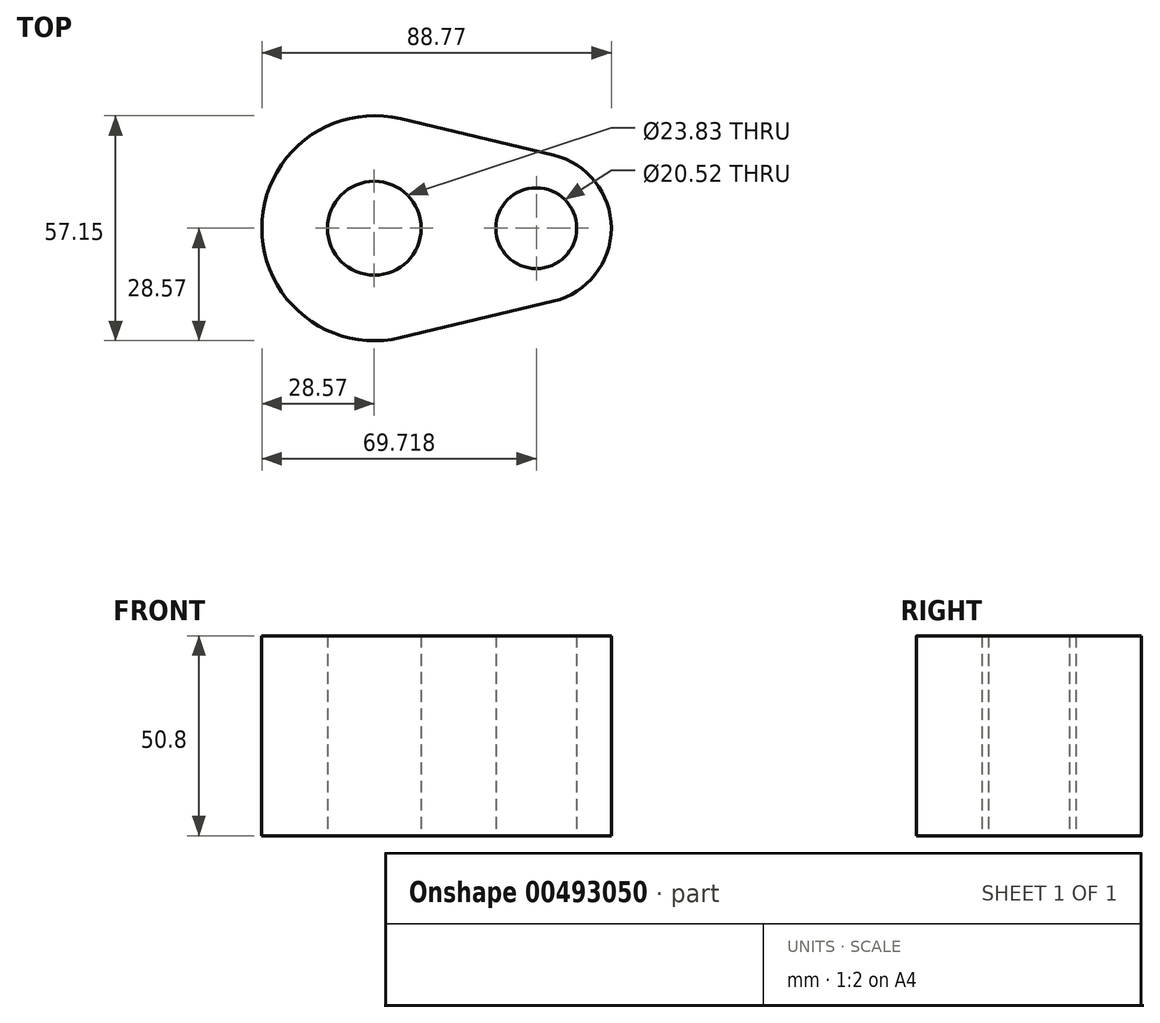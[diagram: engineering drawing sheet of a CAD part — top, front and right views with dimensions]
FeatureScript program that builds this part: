
annotation { "Feature Type Name" : "Feature", "Feature Type Description" : "" }
export const myFeature = defineFeature(function(context is Context, id is Id, definition is map)
    precondition{}
    {
        {
            var Q0;
            Q0=qCreatedBy(makeId("Top.planeOp"),FACE);
            var sketch = newSketch(context, id + "F0", { "sketchPlane" : qUnion([Q0])});
            skArc(sketch, "E0", {"start": v(6.61, 27.8) * mm, "mid": v(-28.57, 0) * mm, "end": v(6.61, -27.8) * mm});
            skArc(sketch, "E1", {"start": v(45.56, -18.53) * mm, "mid": v(60.2, 0) * mm, "end": v(45.56, 18.53) * mm});
            skLineSegment(sketch, "E2", {"start": v(6.61, 27.8) * mm, "end": v(45.56, 18.53) * mm});
            skLineSegment(sketch, "E3", {"start": v(6.61, -27.8) * mm, "end": v(45.56, -18.53) * mm});
            skCircle(sketch, "E4", {"center": v(0, 0) * mm, "radius": 11.92 * mm});
            skCircle(sketch, "E5", {"center": v(41.15, 0) * mm, "radius": 10.26 * mm});
            skSolve(sketch);
        }
        {
            var Q0;
            Q0 = qSketchRegion(id + "F0", true);
            extrude(context, id + "F1", {"entities" : qUnion([Q0]), "depth" : 25.4 * mm, "offsetDistance" : 25.4 * mm});
        }
        {
            var Q0;
            Q0=makeQuery(id+"F1.opExtrude","CAP_FACE",FACE,{"disambiguationData":[OSD([sQuery(id+"F0.wireOp",EDGE,"E0"),sQuery(id+"F0.wireOp",EDGE,"E1"),sQuery(id+"F0.wireOp",EDGE,"E2"),sQuery(id+"F0.wireOp",EDGE,"E3"),sQuery(id+"F0.wireOp",EDGE,"E4"),sQuery(id+"F0.wireOp",EDGE,"E5")])],"isStart":false});
            extrude(context, id + "F2", {"entities" : qUnion([Q0]), "operationType" : NewBodyOperationType.ADD, "oppositeDirection" : true, "depth" : 12.7 * mm, "offsetDistance" : 25.4 * mm});
        }
        {
            var Q0;
            Q0=makeQuery(id+"F1.opExtrude","CAP_FACE",FACE,{"disambiguationData":[OSD([sQuery(id+"F0.wireOp",EDGE,"E0"),sQuery(id+"F0.wireOp",EDGE,"E1"),sQuery(id+"F0.wireOp",EDGE,"E2"),sQuery(id+"F0.wireOp",EDGE,"E3"),sQuery(id+"F0.wireOp",EDGE,"E4"),sQuery(id+"F0.wireOp",EDGE,"E5")])],"isStart":false});
            extrude(context, id + "F3", {"entities" : qUnion([Q0]), "operationType" : NewBodyOperationType.ADD, "depth" : 25.4 * mm, "offsetDistance" : 25.4 * mm});
        }
    });
